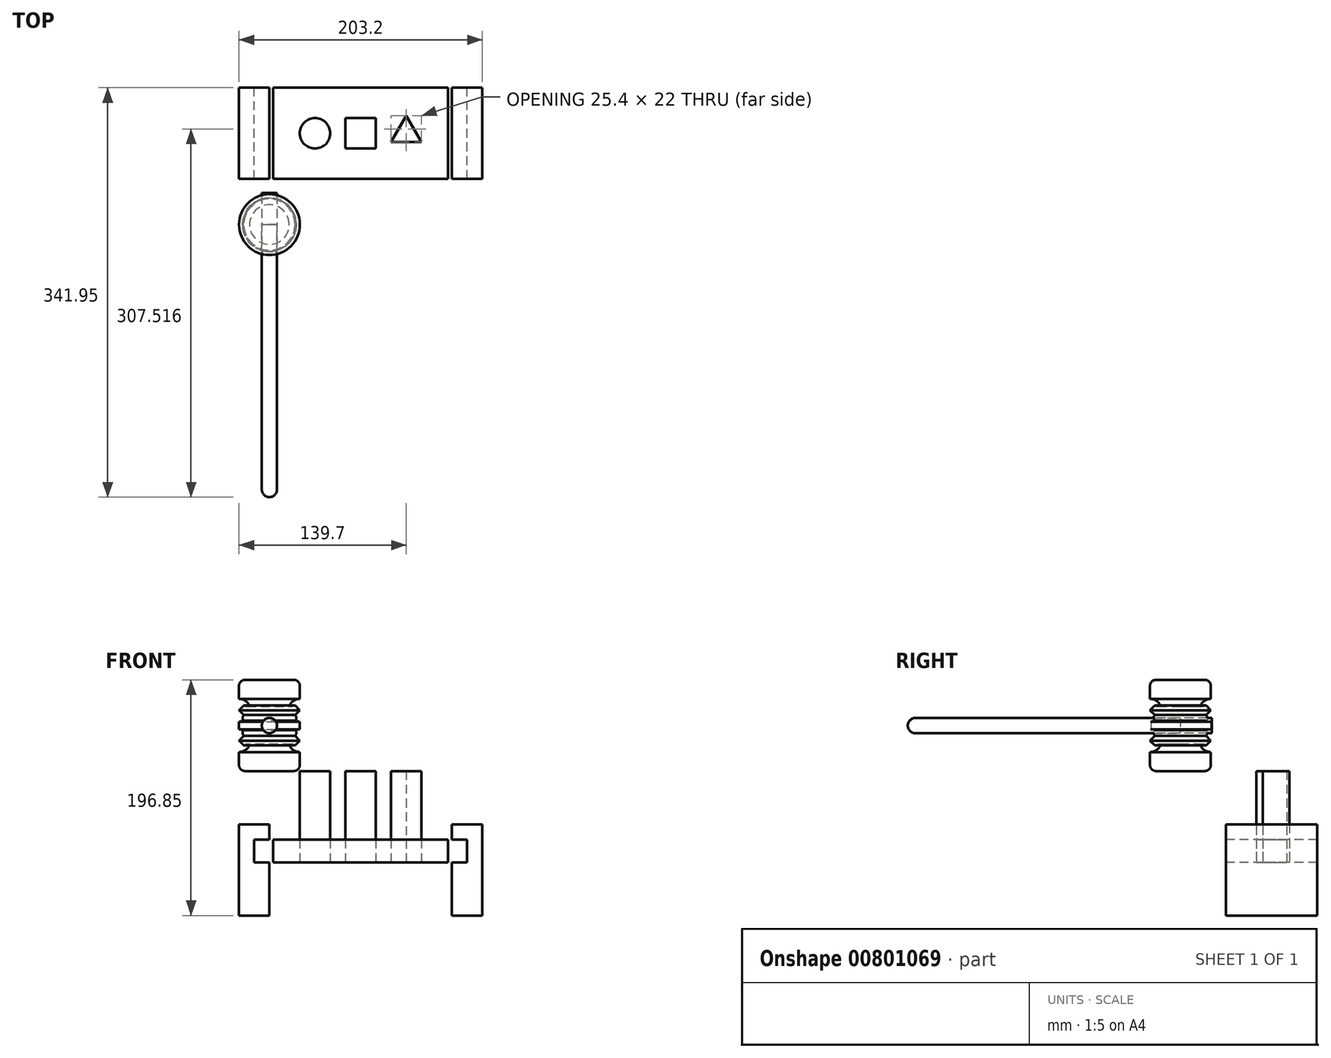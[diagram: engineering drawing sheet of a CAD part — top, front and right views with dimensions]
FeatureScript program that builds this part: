
annotation { "Feature Type Name" : "Feature", "Feature Type Description" : "" }
export const myFeature = defineFeature(function(context is Context, id is Id, definition is map)
    precondition{}
    {
        {
            var Q0;
            Q0=qCreatedBy(makeId("Top.planeOp"),FACE);
            var sketch = newSketch(context, id + "F0", { "sketchPlane" : qUnion([Q0])});
            skLineSegment(sketch, "E0.bottom", {"start": v(-12.7, -12.7) * mm, "end": v(12.7, -12.7) * mm});
            skLineSegment(sketch, "E0.top", {"start": v(-12.7, 12.7) * mm, "end": v(12.7, 12.7) * mm});
            skLineSegment(sketch, "E0.left", {"start": v(-12.7, -12.7) * mm, "end": v(-12.7, 12.7) * mm});
            skLineSegment(sketch, "E0.right", {"start": v(12.7, -12.7) * mm, "end": v(12.7, 12.7) * mm});
            skCircle(sketch, "E1", {"center": v(-38.1, 0) * mm, "radius": 12.7 * mm});
            skCircle(sketch, "E2.cCircle", {"center": v(38.1, 0) * mm, "radius": 7.33 * mm, "construction": true});
            skLineSegment(sketch, "E2.0", {"start": v(38.1, 14.66) * mm, "end": v(50.8, -7.33) * mm});
            skLineSegment(sketch, "E2.1", {"start": v(50.8, -7.33) * mm, "end": v(25.4, -7.33) * mm});
            skLineSegment(sketch, "E2.2", {"start": v(25.4, -7.33) * mm, "end": v(38.1, 14.66) * mm});
            skPoint(sketch, "E2.0.midPoint", {"position": v(44.45, 3.67) * mm});
            skSolve(sketch);
        }
        {
            var Q0;
            Q0=makeQuery(id+"F0.imprint","IMPRINT",FACE,{"disambiguationData":[TD([[makeQuery(id+"F0.imprint","IMPRINT",EDGE,{"derivedFrom":sQuery(id+"F0.wireOp",EDGE,"E0.bottom")}),1.0]])]});
            extrude(context, id + "F1", {"entities" : qUnion([Q0]), "depth" : 76.2 * mm, "offsetDistance" : 25.4 * mm});
        }
        {
            var Q0;
            Q0=makeQuery(id+"F0.imprint","IMPRINT",FACE,{"disambiguationData":[TD([[makeQuery(id+"F0.imprint","IMPRINT",EDGE,{"derivedFrom":sQuery(id+"F0.wireOp",EDGE,"E2.0")}),-1.0]])]});
            extrude(context, id + "F2", {"entities" : qUnion([Q0]), "depth" : 76.2 * mm, "offsetDistance" : 25.4 * mm});
        }
        {
            var Q0;
            Q0=makeQuery(id+"F0.imprint","IMPRINT",FACE,{"disambiguationData":[TD([[makeQuery(id+"F0.imprint","IMPRINT",EDGE,{"derivedFrom":sQuery(id+"F0.wireOp",EDGE,"E1")}),1.0]])]});
            extrude(context, id + "F3", {"entities" : qUnion([Q0]), "depth" : 76.2 * mm, "offsetDistance" : 25.4 * mm});
        }
        {
            var Q0;
            Q0=qCreatedBy(makeId("Top.planeOp"),FACE);
            var sketch = newSketch(context, id + "F4", { "sketchPlane" : qUnion([Q0])});
            skLineSegment(sketch, "E3.bottom", {"start": v(-73.03, 38.1) * mm, "end": v(73.03, 38.1) * mm});
            skLineSegment(sketch, "E3.top", {"start": v(-73.03, -38.1) * mm, "end": v(73.03, -38.1) * mm});
            skLineSegment(sketch, "E3.left", {"start": v(-73.03, 38.1) * mm, "end": v(-73.03, -38.1) * mm});
            skLineSegment(sketch, "E3.right", {"start": v(73.03, 38.1) * mm, "end": v(73.03, -38.1) * mm});
            skCircle(sketch, "E4", {"center": v(-38.1, 0) * mm, "radius": 12.7 * mm});
            skLineSegment(sketch, "E5.bottom", {"start": v(12.7, 12.7) * mm, "end": v(-12.7, 12.7) * mm});
            skLineSegment(sketch, "E5.top", {"start": v(12.7, -12.7) * mm, "end": v(-12.7, -12.7) * mm});
            skLineSegment(sketch, "E5.left", {"start": v(12.7, 12.7) * mm, "end": v(12.7, -12.7) * mm});
            skLineSegment(sketch, "E5.right", {"start": v(-12.7, 12.7) * mm, "end": v(-12.7, -12.7) * mm});
            skPoint(sketch, "E5.middle", {"position": v(0, 0) * mm});
            skCircle(sketch, "E6.cCircle", {"center": v(38.1, 0) * mm, "radius": 7.33 * mm, "construction": true});
            skLineSegment(sketch, "E6.0", {"start": v(38.1, 14.66) * mm, "end": v(50.8, -7.33) * mm});
            skLineSegment(sketch, "E6.1", {"start": v(50.8, -7.33) * mm, "end": v(25.4, -7.33) * mm});
            skLineSegment(sketch, "E6.2", {"start": v(25.4, -7.33) * mm, "end": v(38.1, 14.66) * mm});
            skPoint(sketch, "E6.0.midPoint", {"position": v(44.45, 3.67) * mm});
            skSolve(sketch);
        }
        {
            var Q0;
            Q0 = qSketchRegion(id + "F4", true);
            extrude(context, id + "F5", {"entities" : qUnion([Q0]), "depth" : 19.05 * mm, "offsetDistance" : 25.4 * mm});
        }
        {
            var Q0;
            Q0=qCreatedBy(makeId("Front.planeOp"),FACE);
            var sketch = newSketch(context, id + "F6", { "sketchPlane" : qUnion([Q0])});
            skLineSegment(sketch, "E7.bottom", {"start": v(0, 0) * mm, "end": v(25.4, 0) * mm});
            skLineSegment(sketch, "E7.top", {"start": v(0, 76.2) * mm, "end": v(25.4, 76.2) * mm});
            skLineSegment(sketch, "E7.left", {"start": v(0, 0) * mm, "end": v(0, 76.2) * mm});
            skLineSegment(sketch, "E7.right", {"start": v(25.4, 0) * mm, "end": v(25.4, 76.2) * mm});
            skLineSegment(sketch, "E8.bottom", {"start": v(25.4, 63.5) * mm, "end": v(12.7, 63.5) * mm});
            skLineSegment(sketch, "E8.top", {"start": v(25.4, 44.45) * mm, "end": v(12.7, 44.45) * mm});
            skLineSegment(sketch, "E8.left", {"start": v(25.4, 63.5) * mm, "end": v(25.4, 44.45) * mm});
            skLineSegment(sketch, "E8.right", {"start": v(12.7, 63.5) * mm, "end": v(12.7, 44.45) * mm});
            skSolve(sketch);
        }
        {
            var Q0;
            {var subQ1=sQuery(id+"F6.wireOp",EDGE,"E7.bottom");Q0=makeQuery(id+"F6.imprint","IMPRINT",FACE,{"disambiguationData":[TD([[makeQuery(id+"F6.imprint","IMPRINT",EDGE,{"derivedFrom":subQ1}),1.0]])]});}
            extrude(context, id + "F7", {"entities" : qUnion([Q0]), "depth" : 76.2 * mm, "offsetDistance" : 25.4 * mm});
        }
        {
            var Q0;
            Q0=makeQuery(id+"F7.opExtrude","SWEPT_BODY",BODY,{"disambiguationData":[OSD([sQuery(id+"F6.wireOp",EDGE,"E7.bottom"),sQuery(id+"F6.wireOp",EDGE,"E7.top"),sQuery(id+"F6.wireOp",EDGE,"E7.left"),sQuery(id+"F6.wireOp",EDGE,"E7.right"),sQuery(id+"F6.wireOp",EDGE,"E8.bottom"),sQuery(id+"F6.wireOp",EDGE,"E8.top"),sQuery(id+"F6.wireOp",EDGE,"E8.right")])]});
            transform(context, id + "F8", {"entities" : qUnion([Q0]), "transformType" : TransformType.TRANSLATION_3D, "dx" : -101.6 * mm, "dy" : 38.1 * mm, "dz" : -44.45 * mm, "makeCopy" : false});
        }
        {
            var Q0;
            Q0=makeQuery(id+"F7.opExtrude","SWEPT_BODY",BODY,{"disambiguationData":[OSD([sQuery(id+"F6.wireOp",EDGE,"E7.bottom"),sQuery(id+"F6.wireOp",EDGE,"E7.top"),sQuery(id+"F6.wireOp",EDGE,"E7.left"),sQuery(id+"F6.wireOp",EDGE,"E7.right"),sQuery(id+"F6.wireOp",EDGE,"E8.bottom"),sQuery(id+"F6.wireOp",EDGE,"E8.top"),sQuery(id+"F6.wireOp",EDGE,"E8.right")])]});
            var Q1;
            Q1=qCreatedBy(makeId("Right.planeOp"),FACE);
            mirror(context, id + "F9", {"entities" : qUnion([Q0]), "mirrorPlane" : qUnion([Q1])});
        }
        {
            var Q0;
            Q0=qCreatedBy(makeId("Front.planeOp"),FACE);
            var sketch = newSketch(context, id + "F10", { "sketchPlane" : qUnion([Q0])});
            skLineSegment(sketch, "E9.bottom", {"start": v(0, 0) * mm, "end": v(25.4, 0) * mm});
            skLineSegment(sketch, "E9.top", {"start": v(0, 76.2) * mm, "end": v(25.4, 76.2) * mm});
            skLineSegment(sketch, "E9.left", {"start": v(0, 0) * mm, "end": v(0, 76.2) * mm});
            skLineSegment(sketch, "E9.right", {"start": v(25.4, 0) * mm, "end": v(25.4, 76.2) * mm});
            skCircle(sketch, "E10", {"center": v(25.4, 50.8) * mm, "radius": 9.53 * mm});
            skCircle(sketch, "E11", {"center": v(25.4, 25.4) * mm, "radius": 9.53 * mm});
            skCircle(sketch, "E12", {"center": v(18.66, 32.14) * mm, "radius": 3.81 * mm});
            skCircle(sketch, "E13", {"center": v(18.66, 18.66) * mm, "radius": 3.81 * mm});
            skLineSegment(sketch, "E14", {"start": v(18.66, 32.14) * mm, "end": v(25.4, 25.4) * mm});
            skLineSegment(sketch, "E15", {"start": v(25.4, 25.4) * mm, "end": v(18.66, 18.66) * mm});
            skCircle(sketch, "E16", {"center": v(18.66, 57.54) * mm, "radius": 3.81 * mm});
            skCircle(sketch, "E17", {"center": v(18.66, 44.06) * mm, "radius": 3.81 * mm});
            skLineSegment(sketch, "E18", {"start": v(25.4, 50.8) * mm, "end": v(18.66, 57.54) * mm});
            skLineSegment(sketch, "E19", {"start": v(25.4, 50.8) * mm, "end": v(18.66, 44.06) * mm});
            skPoint(sketch, "E20", {"position": v(0, 38.1) * mm});
            skSolve(sketch);
        }
        {
            var Q0;
            {var subQ13=sQuery(id+"F10.wireOp",EDGE,"E9.bottom");Q0=makeQuery(id+"F10.imprint","IMPRINT",FACE,{"disambiguationData":[TD([[makeQuery(id+"F10.imprint","IMPRINT",EDGE,{"derivedFrom":subQ13}),1.0]])]});}
            var Q1;
            {var subQ0=sQuery(id+"F10.wireOp",EDGE,"E10");var subQ1=makeQuery(id+"F10.imprint","INTERSECT",VERTEX,{"derivedFrom":[subQ0,sQuery(id+"F10.wireOp",EDGE,"E18")]});Q1=makeQuery(id+"F10.imprint","IMPRINT",FACE,{"disambiguationData":[TD([[makeQuery(id+"F10.imprint","IMPRINT",EDGE,{"disambiguationData":[TD([[subQ1,1.0]])],"derivedFrom":subQ0}),-1.0]])]});}
            var Q2;
            {var subQ1=sQuery(id+"F10.wireOp",EDGE,"E10");var subQ7=sQuery(id+"F10.wireOp",EDGE,"E16");var subQ9=makeQuery(id+"F10.imprint","INTERSECT",VERTEX,{"disambiguationData":[OD(1.0)],"derivedFrom":[subQ1,subQ7]});Q2=makeQuery(id+"F10.imprint","IMPRINT",FACE,{"disambiguationData":[TD([[makeQuery(id+"F10.imprint","IMPRINT",EDGE,{"disambiguationData":[TD([[subQ9,-1.0]])],"derivedFrom":subQ1}),1.0]])]});}
            var Q3;
            {var subQ0=sQuery(id+"F10.wireOp",EDGE,"E10");var subQ1=makeQuery(id+"F10.imprint","INTERSECT",VERTEX,{"derivedFrom":[subQ0,sQuery(id+"F10.wireOp",EDGE,"E19")]});Q3=makeQuery(id+"F10.imprint","IMPRINT",FACE,{"disambiguationData":[TD([[makeQuery(id+"F10.imprint","IMPRINT",EDGE,{"disambiguationData":[TD([[subQ1,1.0]])],"derivedFrom":subQ0}),-1.0]])]});}
            var Q4;
            {var subQ0=sQuery(id+"F10.wireOp",EDGE,"E19");var subQ1=sQuery(id+"F10.wireOp",EDGE,"E10");var subQ2=makeQuery(id+"F10.imprint","INTERSECT",VERTEX,{"derivedFrom":[subQ1,subQ0]});Q4=makeQuery(id+"F10.imprint","IMPRINT",FACE,{"disambiguationData":[TD([[makeQuery(id+"F10.imprint","IMPRINT",EDGE,{"disambiguationData":[TD([[subQ2,1.0]])],"derivedFrom":subQ1}),1.0]])]});}
            var Q5;
            {var subQ0=sQuery(id+"F10.wireOp",EDGE,"E19");var subQ1=sQuery(id+"F10.wireOp",EDGE,"E10");var subQ2=makeQuery(id+"F10.imprint","INTERSECT",VERTEX,{"derivedFrom":[subQ1,subQ0]});Q5=makeQuery(id+"F10.imprint","IMPRINT",FACE,{"disambiguationData":[TD([[makeQuery(id+"F10.imprint","IMPRINT",EDGE,{"disambiguationData":[TD([[subQ2,-1.0]])],"derivedFrom":subQ1}),1.0]])]});}
            var Q6;
            {var subQ0=sQuery(id+"F10.wireOp",EDGE,"E11");var subQ1=makeQuery(id+"F10.imprint","INTERSECT",VERTEX,{"derivedFrom":[subQ0,sQuery(id+"F10.wireOp",EDGE,"E14")]});Q6=makeQuery(id+"F10.imprint","IMPRINT",FACE,{"disambiguationData":[TD([[makeQuery(id+"F10.imprint","IMPRINT",EDGE,{"disambiguationData":[TD([[subQ1,1.0]])],"derivedFrom":subQ0}),-1.0]])]});}
            var Q7;
            {var subQ0=sQuery(id+"F10.wireOp",EDGE,"E14");var subQ1=sQuery(id+"F10.wireOp",EDGE,"E11");var subQ2=makeQuery(id+"F10.imprint","INTERSECT",VERTEX,{"derivedFrom":[subQ1,subQ0]});Q7=makeQuery(id+"F10.imprint","IMPRINT",FACE,{"disambiguationData":[TD([[makeQuery(id+"F10.imprint","IMPRINT",EDGE,{"disambiguationData":[TD([[subQ2,-1.0]])],"derivedFrom":subQ1}),1.0]])]});}
            var Q8;
            {var subQ0=sQuery(id+"F10.wireOp",EDGE,"E14");var subQ1=sQuery(id+"F10.wireOp",EDGE,"E11");var subQ2=makeQuery(id+"F10.imprint","INTERSECT",VERTEX,{"derivedFrom":[subQ1,subQ0]});Q8=makeQuery(id+"F10.imprint","IMPRINT",FACE,{"disambiguationData":[TD([[makeQuery(id+"F10.imprint","IMPRINT",EDGE,{"disambiguationData":[TD([[subQ2,1.0]])],"derivedFrom":subQ1}),1.0]])]});}
            var Q9;
            {var subQ3=sQuery(id+"F10.wireOp",EDGE,"E12");var subQ6=sQuery(id+"F10.wireOp",EDGE,"E11");var subQ9=makeQuery(id+"F10.imprint","INTERSECT",VERTEX,{"disambiguationData":[OD(1.0)],"derivedFrom":[subQ6,subQ3]});Q9=makeQuery(id+"F10.imprint","IMPRINT",FACE,{"disambiguationData":[TD([[makeQuery(id+"F10.imprint","IMPRINT",EDGE,{"disambiguationData":[TD([[subQ9,-1.0]])],"derivedFrom":subQ6}),1.0]])]});}
            var Q10;
            {var subQ0=sQuery(id+"F10.wireOp",EDGE,"E11");var subQ1=makeQuery(id+"F10.imprint","INTERSECT",VERTEX,{"derivedFrom":[subQ0,sQuery(id+"F10.wireOp",EDGE,"E15")]});Q10=makeQuery(id+"F10.imprint","IMPRINT",FACE,{"disambiguationData":[TD([[makeQuery(id+"F10.imprint","IMPRINT",EDGE,{"disambiguationData":[TD([[subQ1,1.0]])],"derivedFrom":subQ0}),-1.0]])]});}
            var Q11;
            Q11=sQuery(id+"F10.wireOp",EDGE,"E9.left");
            revolve(context, id + "F11", {"surfaceOperationType" : NewSurfaceOperationType.NEW, "entities" : qUnion([Q0, Q1, Q2, Q3, Q4, Q5, Q6, Q7, Q8, Q9, Q10]), "axis" : qUnion([Q11]), "revolveType" : RevolveType.FULL});
        }
        {
            var Q0;
            Q0=sQuery(id+"F10.wireOp",VERTEX,"E20");
            var Q1;
            Q1=makeQuery(id+"F11.opRevolve","SWEPT_BODY",BODY,{"disambiguationData":[OSD([sQuery(id+"F10.wireOp",EDGE,"E9.bottom"),sQuery(id+"F10.wireOp",EDGE,"E9.top"),sQuery(id+"F10.wireOp",EDGE,"E9.left"),sQuery(id+"F10.wireOp",EDGE,"E9.right"),sQuery(id+"F10.wireOp",EDGE,"E10"),sQuery(id+"F10.wireOp",EDGE,"E11"),sQuery(id+"F10.wireOp",EDGE,"E12"),sQuery(id+"F10.wireOp",EDGE,"E13"),sQuery(id+"F10.wireOp",EDGE,"E14"),sQuery(id+"F10.wireOp",EDGE,"E15"),sQuery(id+"F10.wireOp",EDGE,"E16"),sQuery(id+"F10.wireOp",EDGE,"E17"),sQuery(id+"F10.wireOp",EDGE,"E18"),sQuery(id+"F10.wireOp",EDGE,"E19")])]});
            hole(context, id + "F12", {"style" : HoleStyle.SIMPLE, "endStyle" : HoleEndStyle.THROUGH, "oppositeDirection" : true, "holeDiameter" : 12.7 * mm, "majorDiameter" : 6.35 * mm, "isTappedThrough" : true, "tappedDepth" : 12.7 * mm, "tapClearance" : 3, "locations" : qUnion([Q0]), "scope" : qUnion([Q1])});
        }
        {
            var Q0;
            Q0=makeQuery(id+"F11.opRevolve","SWEPT_EDGE",EDGE,{"disambiguationData":[OSD([sQuery(id+"F10.wireOp",EDGE,"E9.top"),sQuery(id+"F10.wireOp",EDGE,"E9.right")])]});
            var Q1;
            Q1=makeQuery(id+"F11.opRevolve","SWEPT_EDGE",EDGE,{"disambiguationData":[OSD([sQuery(id+"F10.wireOp",EDGE,"E9.bottom"),sQuery(id+"F10.wireOp",EDGE,"E9.right")])]});
            fillet(context, id + "F13", {"entities" : qUnion([Q0, Q1]), "radius" : 5.08 * mm, "tangentPropagation" : true, "allowEdgeOverflow" : false});
        }
        {
            var Q0;
            Q0=qCreatedBy(makeId("Right.planeOp"),FACE);
            var sketch = newSketch(context, id + "F14", { "sketchPlane" : qUnion([Q0])});
            skLineSegment(sketch, "E21.bottom", {"start": v(26.35, 44.31) * mm, "end": v(-221.3, 44.31) * mm});
            skLineSegment(sketch, "E21.top", {"start": v(26.35, 31.61) * mm, "end": v(-221.3, 31.61) * mm});
            skLineSegment(sketch, "E21.left", {"start": v(26.35, 44.31) * mm, "end": v(26.35, 31.61) * mm});
            skLineSegment(sketch, "E21.right", {"start": v(-227.65, 37.96) * mm, "end": v(-227.65, 37.96) * mm});
            skPoint(sketch, "E22.visualSharp", {"position": v(-227.65, 44.31) * mm});
            skArc(sketch, "E22.filletArc", {"start": v(-221.3, 44.31) * mm, "mid": v(-225.79, 42.45) * mm, "end": v(-227.65, 37.96) * mm});
            skPoint(sketch, "E23.visualSharp", {"position": v(-227.65, 31.61) * mm});
            skArc(sketch, "E23.filletArc", {"start": v(-227.65, 37.96) * mm, "mid": v(-225.79, 33.47) * mm, "end": v(-221.3, 31.61) * mm});
            skLineSegment(sketch, "E24", {"start": v(-227.65, 37.96) * mm, "end": v(26.35, 37.96) * mm});
            skSolve(sketch);
        }
        {
            var Q0;
            {var subQ0=sQuery(id+"F14.wireOp",EDGE,"E21.top");Q0=makeQuery(id+"F14.imprint","IMPRINT",FACE,{"disambiguationData":[TD([[makeQuery(id+"F14.imprint","IMPRINT",EDGE,{"derivedFrom":subQ0}),-1.0]])]});}
            var Q1;
            Q1=sQuery(id+"F14.wireOp",EDGE,"E24");
            revolve(context, id + "F15", {"surfaceOperationType" : NewSurfaceOperationType.NEW, "entities" : qUnion([Q0]), "axis" : qUnion([Q1]), "revolveType" : RevolveType.FULL});
        }
        {
            var Q0;
            Q0=makeQuery(id+"F11.opRevolve","SWEPT_BODY",BODY,{"disambiguationData":[OSD([sQuery(id+"F10.wireOp",EDGE,"E9.bottom"),sQuery(id+"F10.wireOp",EDGE,"E9.top"),sQuery(id+"F10.wireOp",EDGE,"E9.left"),sQuery(id+"F10.wireOp",EDGE,"E9.right"),sQuery(id+"F10.wireOp",EDGE,"E10"),sQuery(id+"F10.wireOp",EDGE,"E11"),sQuery(id+"F10.wireOp",EDGE,"E12"),sQuery(id+"F10.wireOp",EDGE,"E13"),sQuery(id+"F10.wireOp",EDGE,"E14"),sQuery(id+"F10.wireOp",EDGE,"E15"),sQuery(id+"F10.wireOp",EDGE,"E16"),sQuery(id+"F10.wireOp",EDGE,"E17"),sQuery(id+"F10.wireOp",EDGE,"E18"),sQuery(id+"F10.wireOp",EDGE,"E19")])]});
            var Q1;
            Q1=makeQuery(id+"F15.opRevolve","SWEPT_BODY",BODY,{"disambiguationData":[OSD([sQuery(id+"F14.wireOp",EDGE,"E21.top"),sQuery(id+"F14.wireOp",EDGE,"E21.left"),sQuery(id+"F14.wireOp",EDGE,"E23.filletArc"),sQuery(id+"F14.wireOp",EDGE,"E24")])]});
            transform(context, id + "F16", {"entities" : qUnion([Q0, Q1]), "transformType" : TransformType.TRANSLATION_3D, "dx" : -76.2 * mm, "dy" : -76.2 * mm, "dz" : 76.2 * mm, "makeCopy" : false});
        }
    });
